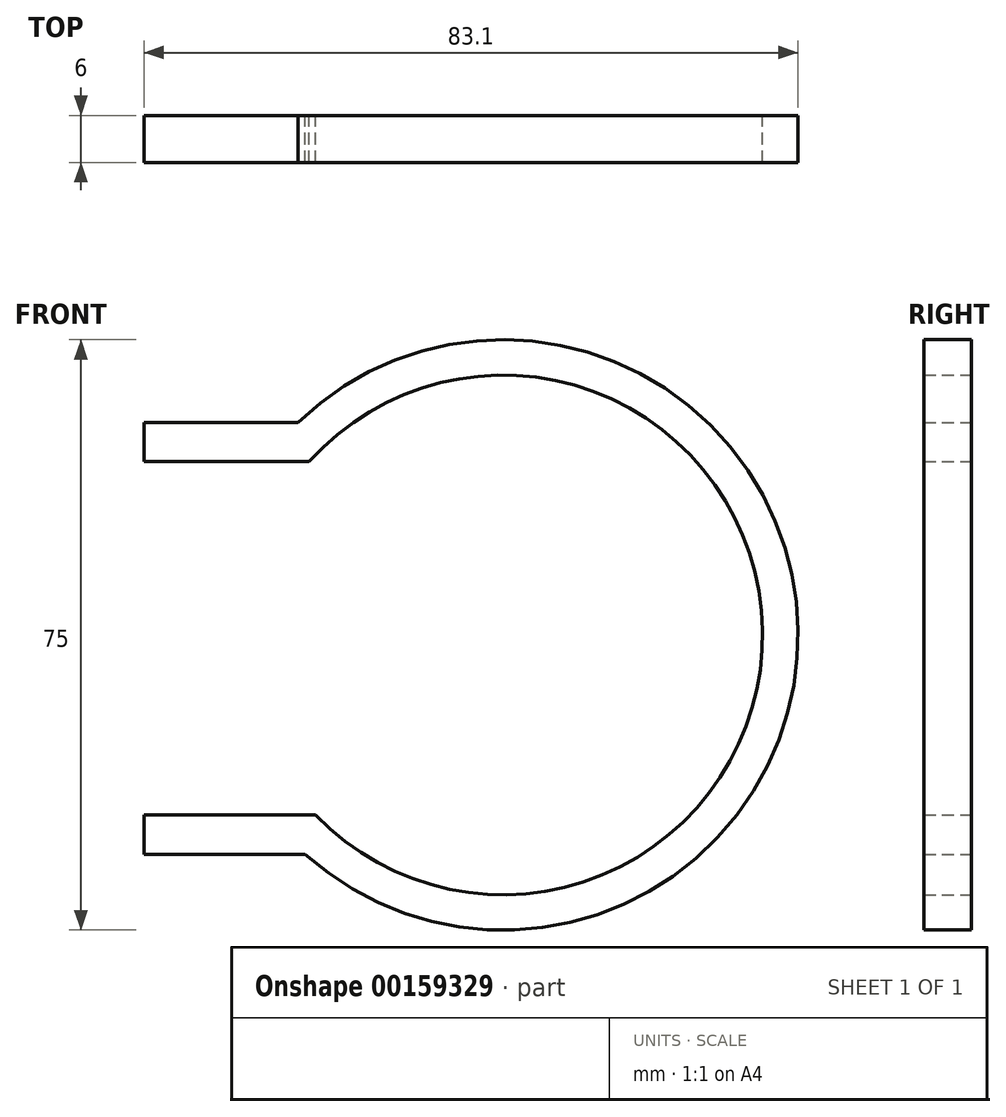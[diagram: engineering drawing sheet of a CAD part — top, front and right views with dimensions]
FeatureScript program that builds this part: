
annotation { "Feature Type Name" : "Feature", "Feature Type Description" : "" }
export const myFeature = defineFeature(function(context is Context, id is Id, definition is map)
    precondition{}
    {
        {
            var Q0;
            Q0=qCreatedBy(makeId("Front.planeOp"),FACE);
            var sketch = newSketch(context, id + "F0", { "sketchPlane" : qUnion([Q0])});
            skLineSegment(sketch, "E0.bottom", {"start": v(-28, 22) * mm, "end": v(-12, 22) * mm});
            skLineSegment(sketch, "E0.top", {"start": v(-28, -22.86) * mm, "end": v(-11.2, -22.86) * mm});
            skArc(sketch, "E1", {"start": v(-11.2, -22.86) * mm, "mid": v(45.6, 0.59) * mm, "end": v(-12, 22) * mm});
            skArc(sketch, "E2", {"start": v(-12.5, -27.86) * mm, "mid": v(50.1, 0.63) * mm, "end": v(-13.43, 27) * mm});
            skLineSegment(sketch, "E3", {"start": v(-13.43, 27) * mm, "end": v(-33, 27) * mm});
            skLineSegment(sketch, "E4", {"start": v(-33, 27) * mm, "end": v(-33, 22) * mm});
            skLineSegment(sketch, "E5", {"start": v(-33, -27.86) * mm, "end": v(-12.5, -27.86) * mm});
            skLineSegment(sketch, "E6", {"start": v(-28, 22) * mm, "end": v(-33, 22) * mm});
            skLineSegment(sketch, "E7", {"start": v(-28, -22.86) * mm, "end": v(-33, -22.86) * mm});
            skLineSegment(sketch, "E8.trimOffspring", {"start": v(-33, -22.86) * mm, "end": v(-33, -27.86) * mm});
            skSolve(sketch);
        }
        {
            var Q0;
            Q0=qSketchRegion(id+"F0",true);
            extrude(context, id + "F1", {"entities" : qUnion([Q0]), "depth" : 6 * mm});
        }
    });
